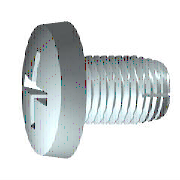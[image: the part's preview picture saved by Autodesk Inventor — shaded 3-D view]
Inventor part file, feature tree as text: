
AUTODESK INVENTOR PART (.ipt)
format: ipt  version: 2024.1 (Build 281209000, 209)  size: 274,944 bytes
history: native  units: mm (DEFAULTED — no unit token found)
features: other x2, extrude x1, plane x1
ambient origin geometry x8: Origin, YZ Plane, XZ Plane, XY Plane, X Axis, Y Axis, Z Axis, Center Point
bodies: Solid1 (feature_tree), Body (feature_tree)
feature tree (4):
  other  "IDS_WORKPLANE{1}"
  extrude  "Slot"  Depth=2.0mm
  other  "Cut"
  plane  "Work Plane3"
